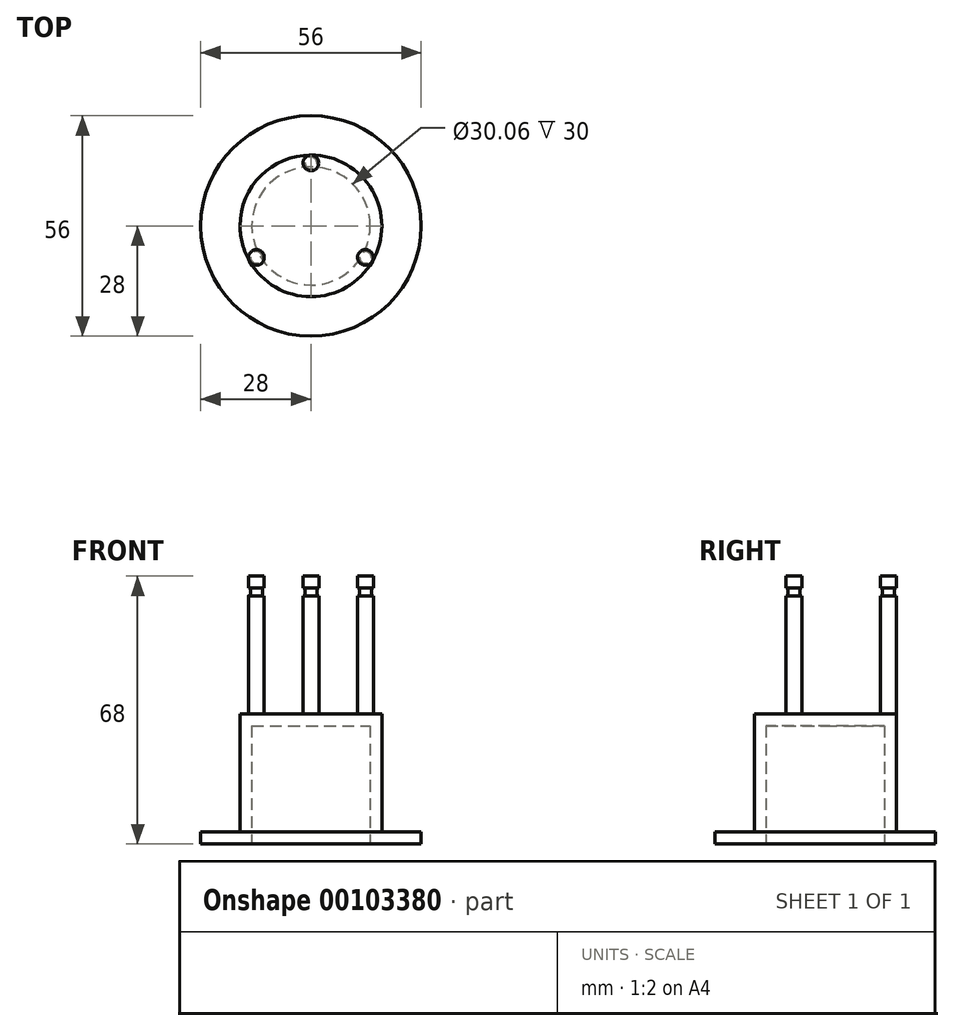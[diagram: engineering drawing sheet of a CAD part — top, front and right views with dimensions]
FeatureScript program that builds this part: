
annotation { "Feature Type Name" : "Feature", "Feature Type Description" : "" }
export const myFeature = defineFeature(function(context is Context, id is Id, definition is map)
    precondition{}
    {
        {
            var Q0;
            Q0=qCreatedBy(makeId("Front.planeOp"),FACE);
            var sketch = newSketch(context, id + "F0", { "sketchPlane" : qUnion([Q0])});
            skLineSegment(sketch, "E0.bottom", {"start": v(18, -3) * mm, "end": v(15.03, -3) * mm});
            skLineSegment(sketch, "E0.top", {"start": v(18, -33) * mm, "end": v(15.03, -33) * mm});
            skLineSegment(sketch, "E0.left", {"start": v(18, -3) * mm, "end": v(18, -33) * mm});
            skLineSegment(sketch, "E0.right", {"start": v(15.03, -3) * mm, "end": v(15.03, -33) * mm});
            skLineSegment(sketch, "E1.bottom", {"start": v(18, -33) * mm, "end": v(28, -33) * mm});
            skLineSegment(sketch, "E1.top", {"start": v(18, -30) * mm, "end": v(28, -30) * mm});
            skLineSegment(sketch, "E1.left", {"start": v(18, -33) * mm, "end": v(18, -30) * mm});
            skLineSegment(sketch, "E1.right", {"start": v(28, -33) * mm, "end": v(28, -30) * mm});
            skLineSegment(sketch, "E2.bottom", {"start": v(18, -3) * mm, "end": v(0, -3) * mm});
            skLineSegment(sketch, "E2.top", {"start": v(18, 0) * mm, "end": v(0, 0) * mm});
            skLineSegment(sketch, "E2.left", {"start": v(18, -3) * mm, "end": v(18, 0) * mm});
            skLineSegment(sketch, "E2.right", {"start": v(0, -3) * mm, "end": v(0, 0) * mm});
            skSolve(sketch);
        }
        {
            var Q0;
            Q0 = qSketchRegion(id + "F0", true);
            var Q1;
            Q1=sQuery(id+"F0.wireOp",EDGE,"E2.right");
            revolve(context, id + "F1", {"entities" : qUnion([Q0]), "axis" : qUnion([Q1]), "revolveType" : RevolveType.FULL});
        }
        {
            var Q0;
            Q0=makeQuery(id+"F1.opRevolve","SWEPT_FACE",FACE,{"disambiguationData":[OSD([sQuery(id+"F0.wireOp",EDGE,"E2.top")])]});
            var sketch = newSketch(context, id + "F2", { "sketchPlane" : qUnion([Q0])});
            skCircle(sketch, "E3", {"center": v(0, 16) * mm, "radius": 2 * mm});
            skCircle(sketch, "E4", {"center": v(13.86, -8) * mm, "radius": 2 * mm});
            skCircle(sketch, "E5", {"center": v(-13.86, -8) * mm, "radius": 2 * mm});
            skLineSegment(sketch, "E6", {"start": v(0, 16) * mm, "end": v(0, 0) * mm});
            skLineSegment(sketch, "E7", {"start": v(0, 0) * mm, "end": v(-13.86, -8) * mm});
            skLineSegment(sketch, "E8", {"start": v(13.86, -8) * mm, "end": v(0, 0) * mm});
            skSolve(sketch);
        }
        {
            var Q0;
            Q0 = qSketchRegion(id + "F2", true);
            extrude(context, id + "F3", {"entities" : qUnion([Q0]), "operationType" : NewBodyOperationType.ADD, "depth" : 30 * mm});
        }
        {
            var Q0;
            Q0=makeQuery(id+"F3.opExtrude","CAP_FACE",FACE,{"disambiguationData":[OSD([sQuery(id+"F2.wireOp",EDGE,"E4")])],"isStart":false});
            var sketch = newSketch(context, id + "F4", { "sketchPlane" : qUnion([Q0])});
            skCircle(sketch, "E9", {"center": v(13.86, -8) * mm, "radius": 1.5 * mm});
            skSolve(sketch);
        }
        {
            var Q0;
            Q0 = qSketchRegion(id + "F4", true);
            extrude(context, id + "F5", {"entities" : qUnion([Q0]), "operationType" : NewBodyOperationType.ADD, "depth" : 2 * mm});
        }
        {
            var Q0;
            Q0=makeQuery(id+"F5.opExtrude","CAP_FACE",FACE,{"disambiguationData":[OSD([sQuery(id+"F4.wireOp",EDGE,"E9")])],"isStart":false});
            var sketch = newSketch(context, id + "F6", { "sketchPlane" : qUnion([Q0])});
            skCircle(sketch, "E10", {"center": v(13.86, -8) * mm, "radius": 2 * mm});
            skSolve(sketch);
        }
        {
            var Q0;
            Q0 = qSketchRegion(id + "F6", true);
            extrude(context, id + "F7", {"entities" : qUnion([Q0]), "operationType" : NewBodyOperationType.ADD, "depth" : 3 * mm});
        }
        {
            var Q0;
            Q0=makeQuery(id+"F3.opExtrude","CAP_FACE",FACE,{"disambiguationData":[OSD([sQuery(id+"F2.wireOp",EDGE,"E3")])],"isStart":false});
            var sketch = newSketch(context, id + "F8", { "sketchPlane" : qUnion([Q0])});
            skCircle(sketch, "E11", {"center": v(0, 16) * mm, "radius": 1.5 * mm});
            skSolve(sketch);
        }
        {
            var Q0;
            Q0 = qSketchRegion(id + "F8", true);
            extrude(context, id + "F9", {"entities" : qUnion([Q0]), "operationType" : NewBodyOperationType.ADD, "depth" : 2 * mm});
        }
        {
            var Q0;
            Q0=makeQuery(id+"F9.opExtrude","CAP_FACE",FACE,{"disambiguationData":[OSD([sQuery(id+"F8.wireOp",EDGE,"E11")])],"isStart":false});
            var sketch = newSketch(context, id + "F10", { "sketchPlane" : qUnion([Q0])});
            skCircle(sketch, "E12", {"center": v(0, 16) * mm, "radius": 2 * mm});
            skSolve(sketch);
        }
        {
            var Q0;
            Q0 = qSketchRegion(id + "F10", true);
            extrude(context, id + "F11", {"entities" : qUnion([Q0]), "operationType" : NewBodyOperationType.ADD, "depth" : 3 * mm});
        }
        {
            var Q0;
            Q0=makeQuery(id+"F3.opExtrude","CAP_FACE",FACE,{"disambiguationData":[OSD([sQuery(id+"F2.wireOp",EDGE,"E5")])],"isStart":false});
            var sketch = newSketch(context, id + "F12", { "sketchPlane" : qUnion([Q0])});
            skCircle(sketch, "E13", {"center": v(-13.86, -8) * mm, "radius": 1.5 * mm});
            skSolve(sketch);
        }
        {
            var Q0;
            Q0 = qSketchRegion(id + "F12", true);
            extrude(context, id + "F13", {"entities" : qUnion([Q0]), "operationType" : NewBodyOperationType.ADD, "depth" : 2 * mm});
        }
        {
            var Q0;
            Q0=makeQuery(id+"F13.opExtrude","CAP_FACE",FACE,{"disambiguationData":[OSD([sQuery(id+"F12.wireOp",EDGE,"E13")])],"isStart":false});
            var sketch = newSketch(context, id + "F14", { "sketchPlane" : qUnion([Q0])});
            skCircle(sketch, "E14", {"center": v(-13.86, -8) * mm, "radius": 2 * mm});
            skSolve(sketch);
        }
        {
            var Q0;
            Q0 = qSketchRegion(id + "F14", true);
            extrude(context, id + "F15", {"entities" : qUnion([Q0]), "operationType" : NewBodyOperationType.ADD, "depth" : 3 * mm});
        }
    });
